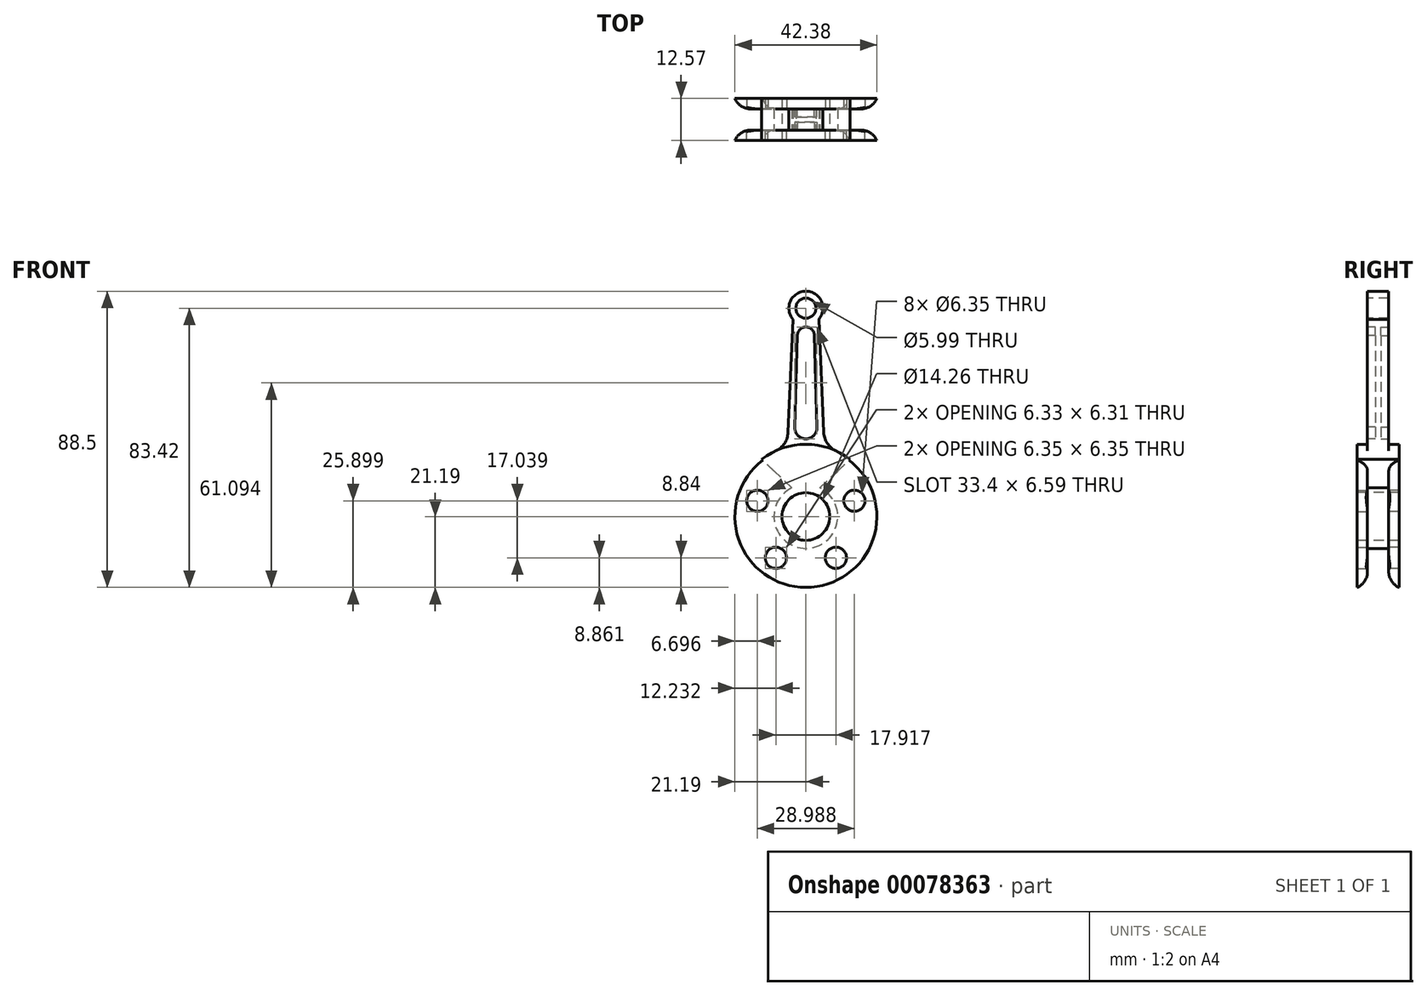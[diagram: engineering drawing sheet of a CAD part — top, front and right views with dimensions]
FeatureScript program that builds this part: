
annotation { "Feature Type Name" : "Feature", "Feature Type Description" : "" }
export const myFeature = defineFeature(function(context is Context, id is Id, definition is map)
    precondition{}
    {
        {
            var Q0;
            Q0=qCreatedBy(makeId("Front.planeOp"),FACE);
            var sketch = newSketch(context, id + "F0", { "sketchPlane" : qUnion([Q0])});
            skCircle(sketch, "E0", {"center": v(0, 0) * mm, "radius": 21.59 * mm});
            skCircle(sketch, "E1", {"center": v(0, 0) * mm, "radius": 15.24 * mm, "construction": true});
            skLineSegment(sketch, "E2", {"start": v(0, 0) * mm, "end": v(28.48, 9.25) * mm, "construction": true});
            skCircle(sketch, "E3", {"center": v(14.5, 4.7) * mm, "radius": 3.18 * mm});
            skLineSegment(sketch, "E4", {"start": v(0, 0) * mm, "end": v(20.34, -28) * mm, "construction": true});
            skCircle(sketch, "E5", {"center": v(8.96, -12.33) * mm, "radius": 3.18 * mm});
            skCircle(sketch, "E6.MirrorC", {"center": v(-14.5, 4.7) * mm, "radius": 3.18 * mm});
            skCircle(sketch, "E7.MirrorC", {"center": v(-8.96, -12.33) * mm, "radius": 3.18 * mm});
            skCircle(sketch, "E8", {"center": v(0, 0) * mm, "radius": 7.13 * mm});
            skSolve(sketch);
        }
        {
            var Q0;
            Q0 = qSketchRegion(id + "F0", true);
            extrude(context, id + "F1", {"entities" : qUnion([Q0]), "depth" : 3.1 * mm});
        }
        {
            var Q0;
            Q0=makeQuery(id+"F1.opExtrude","CAP_FACE",FACE,{"disambiguationData":[OSD([sQuery(id+"F0.wireOp",EDGE,"E0"),sQuery(id+"F0.wireOp",EDGE,"E3"),sQuery(id+"F0.wireOp",EDGE,"E5"),sQuery(id+"F0.wireOp",EDGE,"E6.MirrorC"),sQuery(id+"F0.wireOp",EDGE,"E7.MirrorC"),sQuery(id+"F0.wireOp",EDGE,"E8")])],"isStart":true});
            var sketch = newSketch(context, id + "F2", { "sketchPlane" : qUnion([Q0])});
            skArc(sketch, "E9", {"start": v(-4.17, 8.56) * mm, "mid": v(0, -9.53) * mm, "end": v(4.17, 8.56) * mm});
            skLineSegment(sketch, "E10", {"start": v(4.17, 8.56) * mm, "end": v(13.2, 17.08) * mm});
            skLineSegment(sketch, "E11.MirrorCS", {"start": v(-4.17, 8.56) * mm, "end": v(-13.2, 17.08) * mm});
            skPoint(sketch, "E12.orphan", {"position": v(0, 4.63) * mm});
            skLineSegment(sketch, "E13", {"start": v(0, 0) * mm, "end": v(0, 62.23) * mm, "construction": true});
            skArc(sketch, "E14", {"start": v(3.85, 58.92) * mm, "mid": v(0, 67.31) * mm, "end": v(-3.85, 58.92) * mm});
            skCircle(sketch, "E15", {"center": v(0, 62.23) * mm, "radius": 3 * mm});
            skLineSegment(sketch, "E16", {"start": v(-3.85, 58.92) * mm, "end": v(-5.33, 25.1) * mm});
            skLineSegment(sketch, "E17.MirrorCS", {"start": v(3.85, 58.92) * mm, "end": v(5.33, 25.1) * mm});
            skPoint(sketch, "E18.newPointA", {"position": v(5.52, 20.87) * mm});
            skArc(sketch, "E18.filletArc", {"start": v(5.33, 25.1) * mm, "mid": v(6.4, 21.84) * mm, "end": v(9.02, 19.61) * mm});
            skArc(sketch, "E19", {"start": v(13.2, 17.08) * mm, "mid": v(11.19, 18.47) * mm, "end": v(9.02, 19.61) * mm});
            skArc(sketch, "E20.trimOffspring", {"start": v(-9.02, 19.61) * mm, "mid": v(-11.19, 18.47) * mm, "end": v(-13.2, 17.08) * mm});
            skPoint(sketch, "E21.visualSharp", {"position": v(-5.52, 20.87) * mm});
            skArc(sketch, "E21.filletArc", {"start": v(-9.02, 19.61) * mm, "mid": v(-6.4, 21.84) * mm, "end": v(-5.33, 25.1) * mm});
            skCircle(sketch, "E22", {"center": v(0, 0) * mm, "radius": 7.13 * mm});
            skSolve(sketch);
        }
        {
            var Q0;
            Q0 = qSketchRegion(id + "F2", true);
            extrude(context, id + "F3", {"entities" : qUnion([Q0]), "depth" : 6.35 * mm});
        }
        {
            var Q0;
            Q0=qCreatedBy(makeId("Front.planeOp"),FACE);
            cPlane(context, id + "F4", {"entities" : qUnion([Q0]), "cplaneType" : CPlaneType.OFFSET, "offset" : 3.17 * mm, "oppositeDirection" : true, "width" : 152.4 * mm, "height" : 152.4 * mm});
        }
        {
            var Q0;
            Q0=makeQuery(id+"F1.opExtrude","SWEPT_BODY",BODY,{"disambiguationData":[OSD([sQuery(id+"F0.wireOp",EDGE,"E0"),sQuery(id+"F0.wireOp",EDGE,"E3"),sQuery(id+"F0.wireOp",EDGE,"E5"),sQuery(id+"F0.wireOp",EDGE,"E6.MirrorC"),sQuery(id+"F0.wireOp",EDGE,"E7.MirrorC"),sQuery(id+"F0.wireOp",EDGE,"E8")])]});
            var Q1;
            Q1=qCreatedBy(id+"F4.planeOp",FACE);
            mirror(context, id + "F5", {"operationType" : NewBodyOperationType.ADD, "entities" : qUnion([Q0]), "mirrorPlane" : qUnion([Q1])});
        }
        {
            var Q0;
            Q0=makeQuery(id+"F3.opExtrude","CAP_FACE",FACE,{"disambiguationData":[OSD([sQuery(id+"F2.wireOp",EDGE,"E9"),sQuery(id+"F2.wireOp",EDGE,"E10"),sQuery(id+"F2.wireOp",EDGE,"E11.MirrorCS"),sQuery(id+"F2.wireOp",EDGE,"E14"),sQuery(id+"F2.wireOp",EDGE,"E15"),sQuery(id+"F2.wireOp",EDGE,"E16"),sQuery(id+"F2.wireOp",EDGE,"E17.MirrorCS"),sQuery(id+"F2.wireOp",EDGE,"E18.filletArc"),sQuery(id+"F2.wireOp",EDGE,"E19"),sQuery(id+"F2.wireOp",EDGE,"E20.trimOffspring"),sQuery(id+"F2.wireOp",EDGE,"E21.filletArc"),sQuery(id+"F2.wireOp",EDGE,"E22")])],"isStart":true});
            var sketch = newSketch(context, id + "F6", { "sketchPlane" : qUnion([Q0])});
            skArc(sketch, "E23", {"start": v(-3.3, 26.69) * mm, "mid": v(0, 23.2) * mm, "end": v(3.3, 26.69) * mm});
            skArc(sketch, "E24", {"start": v(2.54, 54.06) * mm, "mid": v(0, 56.6) * mm, "end": v(-2.54, 54.06) * mm});
            skLineSegment(sketch, "E25", {"start": v(-2.54, 54.06) * mm, "end": v(-3.3, 26.5) * mm});
            skLineSegment(sketch, "E26.MirrorCS", {"start": v(2.54, 54.06) * mm, "end": v(3.3, 26.5) * mm});
            skSolve(sketch);
        }
        {
            var Q0;
            Q0 = qSketchRegion(id + "F6", true);
            extrude(context, id + "F7", {"entities" : qUnion([Q0]), "oppositeDirection" : true, "depth" : 2.4 * mm});
        }
        {
            var Q0;
            Q0=qCreatedBy(id+"F4.planeOp",FACE);
            var sketch = newSketch(context, id + "F8", { "sketchPlane" : qUnion([Q0])});
            skLineSegment(sketch, "E27", {"start": v(0, 52.42) * mm, "end": v(0, 35.93) * mm, "construction": true});
            skSolve(sketch);
        }
        {
            var Q0;
            Q0=makeQuery(id+"F7.opExtrude","SWEPT_BODY",BODY,{"disambiguationData":[OSD([sQuery(id+"F6.wireOp",EDGE,"E23"),sQuery(id+"F6.wireOp",EDGE,"E24"),sQuery(id+"F6.wireOp",EDGE,"E25"),sQuery(id+"F6.wireOp",EDGE,"E26.MirrorCS")])]});
            var Q1;
            Q1=sQuery(id+"F8.wireOp",EDGE,"E27");
            circularPattern(context, id + "F9", {"operationType" : NewBodyOperationType.REMOVE, "entities" : qUnion([Q0]), "axis" : qUnion([Q1]), "angle" : 180 * degree, "instanceCount" : 2});
        }
        {
            var Q0;
            {var subQ1=sQuery(id+"F2.wireOp",EDGE,"E18.filletArc");var subQ4=sQuery(id+"F0.wireOp",EDGE,"E0");Q0=makeQuery(id+"F5.boolean.opBoolean","SPLIT",EDGE,{"disambiguationData":[TD([makeQuery(id+"F3.opExtrude","SWEPT_FACE",FACE,{"disambiguationData":[OSD([subQ1])]})])],"derivedFrom":makeQuery(id+"F5.opPattern","COPY",EDGE,{"derivedFrom":makeQuery(id+"F1.opExtrude","CAP_EDGE",EDGE,{"disambiguationData":[OSD([subQ4])],"isStart":true}),"instanceName":"1"})});}
            var Q1;
            {var subQ1=sQuery(id+"F2.wireOp",EDGE,"E18.filletArc");var subQ4=sQuery(id+"F0.wireOp",EDGE,"E0");Q1=makeQuery(id+"F5.boolean.opBoolean","SPLIT",EDGE,{"disambiguationData":[TD([makeQuery(id+"F3.opExtrude","SWEPT_FACE",FACE,{"disambiguationData":[OSD([subQ1])]})])],"derivedFrom":makeQuery(id+"F1.opExtrude","CAP_EDGE",EDGE,{"disambiguationData":[OSD([subQ4])],"isStart":true})});}
            fillet(context, id + "F10", {"entities" : qUnion([Q0, Q1]), "radius" : 5.08 * mm, "tangentPropagation" : true, "allowEdgeOverflow" : false});
        }
    });
